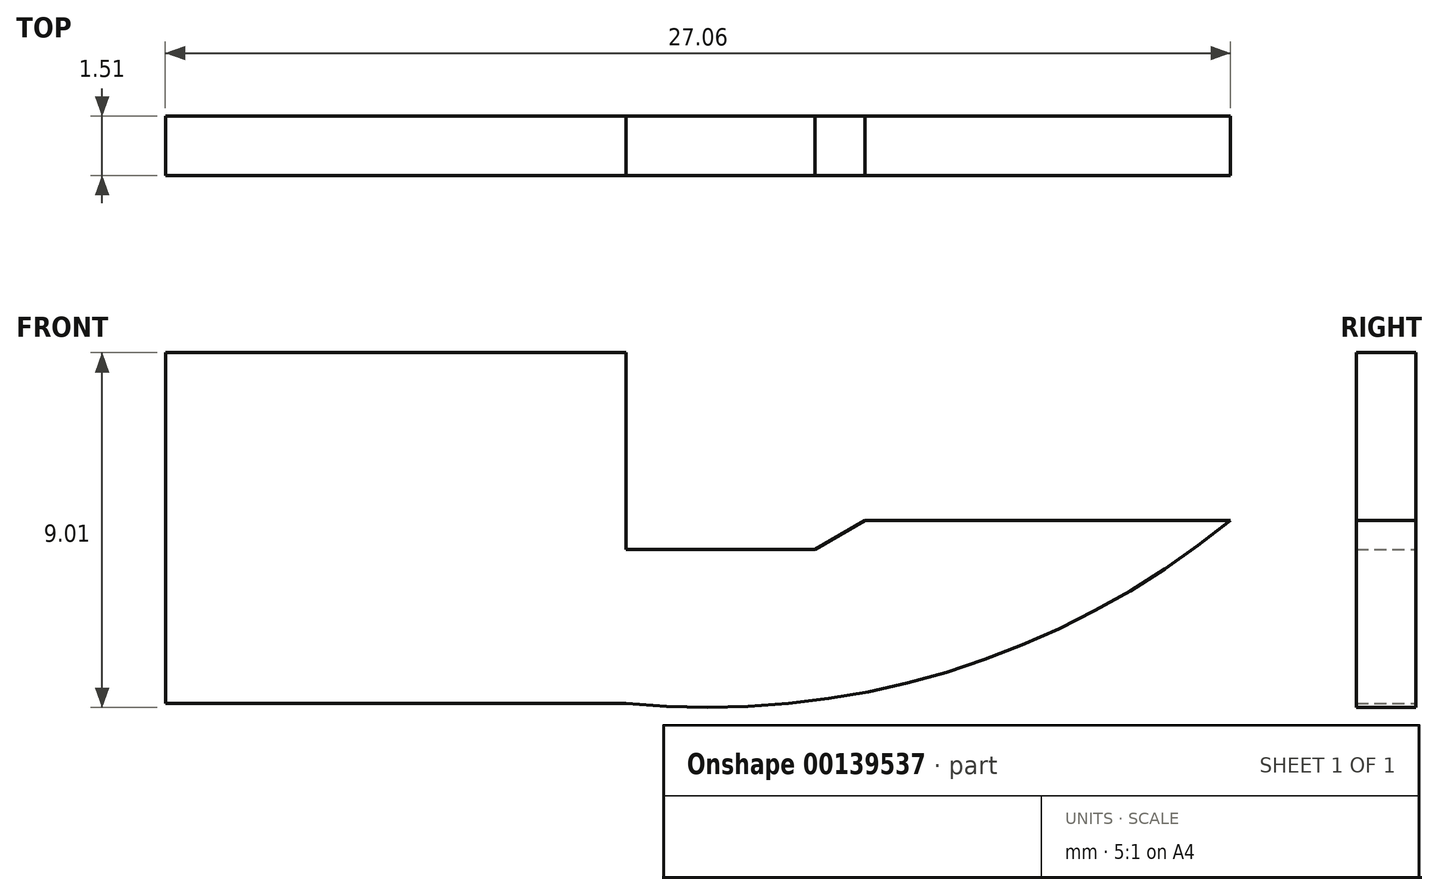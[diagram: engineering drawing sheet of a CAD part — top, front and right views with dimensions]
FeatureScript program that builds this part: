
annotation { "Feature Type Name" : "Feature", "Feature Type Description" : "" }
export const myFeature = defineFeature(function(context is Context, id is Id, definition is map)
    precondition{}
    {
        {
            var Q0;
            Q0=qCreatedBy(makeId("Front.planeOp"),FACE);
            var sketch = newSketch(context, id + "F0", { "sketchPlane" : qUnion([Q0])});
            skLineSegment(sketch, "E0", {"start": v(-16.86, 36.88) * mm, "end": v(-16.86, 31.88) * mm});
            skLineSegment(sketch, "E1", {"start": v(-16.86, 31.88) * mm, "end": v(-12.06, 31.88) * mm});
            skLineSegment(sketch, "E2", {"start": v(-12.06, 31.88) * mm, "end": v(-10.78, 32.62) * mm});
            skLineSegment(sketch, "E3", {"start": v(-10.78, 32.62) * mm, "end": v(-1.5, 32.62) * mm});
            skLineSegment(sketch, "E4", {"start": v(-28.56, 36.88) * mm, "end": v(-28.56, 26.88) * mm});
            skArc(sketch, "E5", {"start": v(-16.86, 27.97) * mm, "mid": v(-8.72, 28.76) * mm, "end": v(-1.5, 32.62) * mm});
            skLineSegment(sketch, "E6", {"start": v(-28.56, 36.88) * mm, "end": v(-16.86, 36.88) * mm});
            skLineSegment(sketch, "E7", {"start": v(-16.86, 27.97) * mm, "end": v(-28.56, 27.97) * mm});
            skLineSegment(sketch, "E8", {"start": v(-28.56, 26.88) * mm, "end": v(-28.56, 27.97) * mm});
            skSolve(sketch);
        }
        {
            var Q0;
            Q0=makeQuery(id+"F0.imprint","IMPRINT",FACE,{"disambiguationData":[TD([[makeQuery(id+"F0.imprint","IMPRINT",EDGE,{"derivedFrom":sQuery(id+"F0.wireOp",EDGE,"E0")}),-1.0]])]});
            extrude(context, id + "F1", {"entities" : qUnion([Q0]), "depth" : 1.51 * mm});
        }
    });
